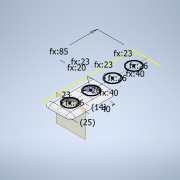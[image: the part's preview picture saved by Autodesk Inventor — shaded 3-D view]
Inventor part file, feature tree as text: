
AUTODESK INVENTOR PART (.ipt)
format: ipt  version: 2021 (Build 250183000, 183)  size: 2,192,896 bytes
history: native  units: in
note: dims shown in document units (in); Inventor stores cm internally (conversion verified against a paired STEP export)
features: extrude x11, other x9, fillet x3, sketch x2
ambient origin geometry x8: Origin, YZ Plane, XZ Plane, XY Plane, X Axis, Y Axis, Z Axis, Center Point
bodies: Body1 (feature_tree)
feature tree (25):
  extrude  "Base"  Depth=2.0472in
  other  "Top Indent Sketch"
  extrude  "Top"  Depth=1.0236in
  extrude  "Walls"  Depth=1.0236in
  fillet  "Outer"  Radius=1.0236in
  extrude  "Outer Wire"  Depth=1.0236in
  extrude  "Wall Holes"  Depth=1.5748in
  extrude  "Text"  Depth=1.5748in
  extrude  "Inner Sketch"  Depth=1.5748in
  fillet  "Inner Fillet"  Radius=0.7087in
  extrude  "halfer"  Depth=0.315in
  extrude  "Top Indent"  Depth=0.315in
  other  "Wire Hole Plane"
  extrude  "Wire Hole"  Depth=0.2362in
  fillet  "Fillet9"  Radius=0.2362in
  extrude  "Extrusion20"  Depth=1.4567in
  other  "Base Sketch"
  other  "Walls Sketch"
  other  "Outer Wire Sketch"
  other  "Wall Holes Sketch"
  other  "Text Sketch"
  other  "Inner Support Sketch"
  sketch  "Sketch25"  dims[d6=6.6929in d7=2.0472in]
  other  "Wire Hole Sketch"
  sketch  "Sketch28"  dims[d8=1.7717in d9=0.0in d10=1.0236in d11=1.0236in d12=1.0236in d13=1.0236in d14=1.5748in d15=1.5748in d16=1.5748in d19=0.7087in d20=0.0in d21=0.315in d22=0.315in d23=0.2362in d24=0.2362in d25=1.4567in d26=0.0in d27=0.9055in d28=0.9055in d29=0.9055in d30=0.9055in d31=0.7874in d32=3.3465in d33=1.5748in d35=0.9843in d36=0.3937in d38=0.3937in d39=0.0in d52=0.315in d55=0.1969in d56=0.0in d58=0.5512in d65=0.315in d66=0.1575in d67=0.1575in d68=0.315in d69=0.2774in d70=0.2774in d71=0.0499in d72=0.0499in d73=1.6535in d74=0.0in d77=0.6496in d81=0.9843in d82=0.0in d85=0.5906in d86=0.1575in d87=0.1575in d88=1.0236in d89=0.315in d90=0.1575in d92=0.0in d93=0.1181in d94=0.0in d95=0.1575in d96=0.6496in d143=0.0in d144=0.0in d155=3.3465in d156=0.0in d158=0.0945in d159=0.0in d162=0.2362in d163=0.0in d164=0.0in d165=0.1969in d166=0.2362in d167=0.0in d168=0.1969in d169=0.1969in d170=4.7244in d171=0.0in d172=3.3465in d173=1.0236in d174=0.0394in d175=1.2992in d176=1.5748in d177=0.0in d44=0.0197in d45=0.0344in d46=0.0197in d47=0.0344in d48=0.0197in d49=0.0344in d59=0.0197in d60=0.0344in d61=0.0197in d62=0.0344in d178=0.0344in]
